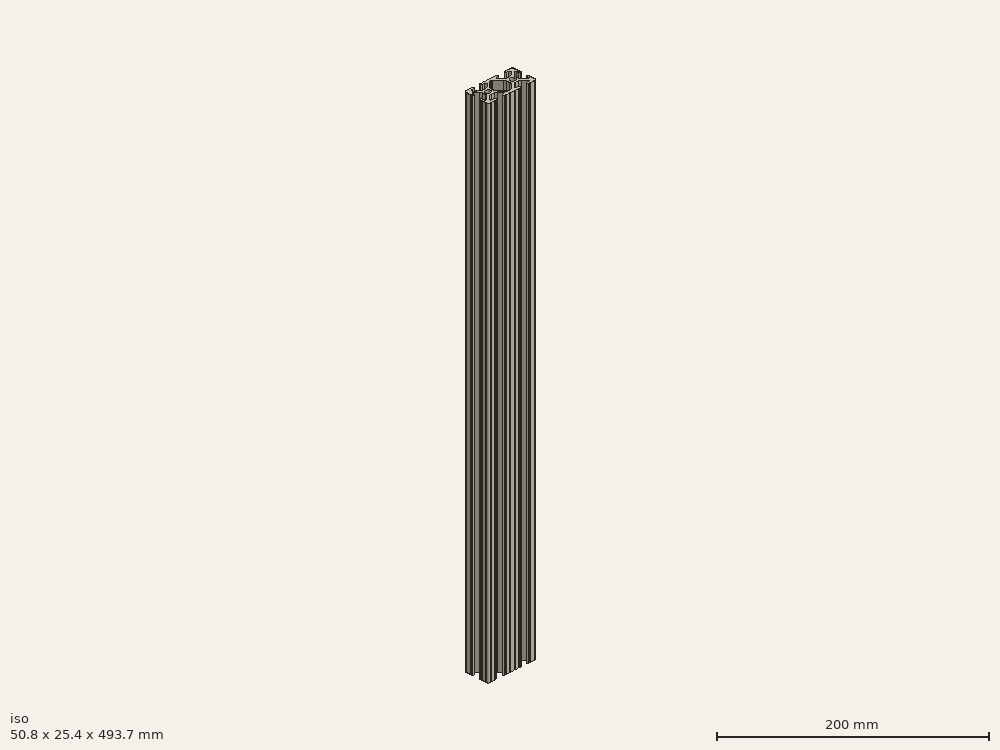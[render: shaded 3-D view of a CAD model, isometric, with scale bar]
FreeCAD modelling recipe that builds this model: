
FCSTD DOCUMENT  (FreeCAD 0.18R4 (GitTag))
Label: 1020-19p438
License: All rights reserved
LicenseURL: http://en.wikipedia.org/wiki/All_rights_reserved
objects: Sketcher::SketchObject×1, Part::Extrusion×1
note: 2 computed .brp shape members not serialized (recipe doc carries the construction recipe); baked Part::Feature solids carry a one-line shape summary decoded from their .brp

FEATURE [Sketcher::SketchObject] Sketch162
  sketch-geometry (162):
    g0: LineSegment StartX=7.25951 StartY=3.86941 StartZ=0 EndX=1.54575 EndY=9.57277 EndZ=0
    g1: LineSegment StartX=8.41248 StartY=-10.4902 StartZ=0 EndX=6.28364 EndY=-10.4902 EndZ=0
    g2: ArcOfCircle CenterX=8.41255 CenterY=-11.651 CenterZ=0 NormalX=0 NormalY=0 NormalZ=1 AngleXU=0 Radius=1.04895 StartAngle=4.71239 EndAngle=6.28319
    g3: LineSegment StartX=5.53258 StartY=-8.66607 StartZ=0 EndX=8.80999 EndY=-5.41626 EndZ=0
    g4: LineSegment StartX=9.4615 StartY=-11.651 StartZ=0 EndX=9.4615 EndY=-11.5392 EndZ=0
    g5: ArcOfCircle CenterX=8.41248 CenterY=-11.5392 CenterZ=0 NormalX=0 NormalY=0 NormalZ=1 AngleXU=0 Radius=1.04902 StartAngle=1.15714e-07 EndAngle=1.5708
    g6: ArcOfCircle CenterX=6.28364 CenterY=-9.42351 CenterZ=0 NormalX=0 NormalY=0 NormalZ=1 AngleXU=0 Radius=1.06669 StartAngle=2.35197 EndAngle=4.71239
    g7: LineSegment StartX=-7.28286 StartY=-3.84586 StartZ=0 EndX=-1.67557 EndY=-9.56109 EndZ=0
    g8: LineSegment StartX=1.50403 StartY=-9.57645 StartZ=0 EndX=7.25205 EndY=-3.87684 EndZ=0
    g9: LineSegment StartX=-0.551457 StartY=-10.033 StartZ=0 EndX=0.3952 EndY=-10.033 EndZ=0
    g10: LineSegment StartX=-1.54575 StartY=9.57277 StartZ=0 EndX=-7.25951 EndY=3.86941 EndZ=0
    g11: ArcOfCircle CenterX=0.3952 CenterY=-8.4582 CenterZ=0 NormalX=0 NormalY=0 NormalZ=1 AngleXU=0 Radius=1.5748 StartAngle=4.71239 EndAngle=5.49356
    g12: ArcOfCircle CenterX=5.0165 CenterY=-1.6223 CenterZ=0 NormalX=0 NormalY=0 NormalZ=1 AngleXU=0 Radius=3.175 StartAngle=5.49356 EndAngle=6.28319
    g13: LineSegment StartX=8.1915 StartY=-1.6223 StartZ=0 EndX=8.1915 EndY=1.6223 EndZ=0
    g14: LineSegment StartX=0.433213 StartY=10.033 StartZ=0 EndX=-0.433213 EndY=10.033 EndZ=0
    g15: ArcOfCircle CenterX=-0.551456 CenterY=-8.4582 CenterZ=0 NormalX=0 NormalY=0 NormalZ=1 AngleXU=0 Radius=1.5748 StartAngle=3.91746 EndAngle=4.71239
    g16: ArcOfCircle CenterX=-5.0165 CenterY=1.6223 CenterZ=0 NormalX=0 NormalY=0 NormalZ=1 AngleXU=0 Radius=3.175 StartAngle=2.35528 EndAngle=3.14159
    g17: ArcOfCircle CenterX=-0.433213 CenterY=8.4582 CenterZ=0 NormalX=0 NormalY=0 NormalZ=1 AngleXU=0 Radius=1.5748 StartAngle=1.5708 EndAngle=2.35528
    g18: ArcOfCircle CenterX=5.0165 CenterY=1.6223 CenterZ=0 NormalX=0 NormalY=0 NormalZ=1 AngleXU=0 Radius=3.175 StartAngle=2.15656e-07 EndAngle=0.78631
    g19: Circle CenterX=12.7 CenterY=-2.5e-15 CenterZ=0 NormalX=0 NormalY=0 NormalZ=-1 AngleXU=0 Radius=2.6035
    g20: Circle CenterX=-12.7 CenterY=2.5e-15 CenterZ=0 NormalX=0 NormalY=0 NormalZ=-1 AngleXU=0 Radius=2.6035
    g21: LineSegment StartX=-8.1915 StartY=1.6223 StartZ=0 EndX=-8.1915 EndY=-1.6223 EndZ=0
    g22: LineSegment StartX=-2.13358 StartY=-12.7 StartZ=0 EndX=2.13358 EndY=-12.7 EndZ=0
    g23: ArcOfCircle CenterX=-5.0165 CenterY=-1.6223 CenterZ=0 NormalX=0 NormalY=0 NormalZ=1 AngleXU=0 Radius=3.175 StartAngle=3.14159 EndAngle=3.91746
    g24: LineSegment StartX=3.14958 StartY=-12.7 StartZ=0 EndX=6.3669 EndY=-12.7 EndZ=0
    g25: ArcOfCircle CenterX=6.8749 CenterY=-12.7 CenterZ=0 NormalX=0 NormalY=0 NormalZ=1 AngleXU=0 Radius=0.508 StartAngle=0 EndAngle=3.14159
    g26: LineSegment StartX=-6.28939 StartY=-10.4902 StartZ=0 EndX=-8.41248 EndY=-10.4902 EndZ=0
    g27: LineSegment StartX=-8.41255 StartY=-12.7 StartZ=0 EndX=-7.38288 EndY=-12.7 EndZ=0
    g28: ArcOfCircle CenterX=0.433213 CenterY=8.4582 CenterZ=0 NormalX=0 NormalY=0 NormalZ=1 AngleXU=0 Radius=1.5748 StartAngle=0.78631 EndAngle=1.5708
    g29: ArcOfCircle CenterX=2.64158 CenterY=-12.7 CenterZ=0 NormalX=0 NormalY=0 NormalZ=1 AngleXU=0 Radius=0.508 StartAngle=0 EndAngle=3.14159
    g30: ArcOfCircle CenterX=-16.9875 CenterY=-11.5392 CenterZ=0 NormalX=0 NormalY=0 NormalZ=1 AngleXU=0 Radius=1.04902 StartAngle=1.16223e-07 EndAngle=1.5708
    g31: LineSegment StartX=-8.81696 StartY=-5.44724 StartZ=0 EndX=-5.56415 EndY=-8.76265 EndZ=0
    g32: LineSegment StartX=-16.9875 StartY=-10.4902 StartZ=0 EndX=-19.1164 EndY=-10.4902 EndZ=0
    g33: ArcOfCircle CenterX=-11.0833 CenterY=-7.6708 CenterZ=0 NormalX=0 NormalY=0 NormalZ=1 AngleXU=0 Radius=3.175 StartAngle=0.775866 EndAngle=1.5708
    g34: ArcOfCircle CenterX=-14.3449 CenterY=-7.6708 CenterZ=0 NormalX=0 NormalY=0 NormalZ=1 AngleXU=0 Radius=3.175 StartAngle=1.5708 EndAngle=2.3692
    g35: ArcOfCircle CenterX=-19.1164 CenterY=-9.4742 CenterZ=0 NormalX=0 NormalY=0 NormalZ=1 AngleXU=0 Radius=1.016 StartAngle=2.3692 EndAngle=4.71239
    g36: ArcOfCircle CenterX=-8.41248 CenterY=-11.5392 CenterZ=0 NormalX=0 NormalY=0 NormalZ=1 AngleXU=0 Radius=1.04902 StartAngle=1.5708 EndAngle=3.14159
    g37: LineSegment StartX=7.3829 StartY=-12.7 StartZ=0 EndX=8.41255 EndY=-12.7 EndZ=0
    g38: ArcOfCircle CenterX=-8.41255 CenterY=-11.651 CenterZ=0 NormalX=0 NormalY=0 NormalZ=1 AngleXU=0 Radius=1.04895 StartAngle=3.14159 EndAngle=4.71239
    g39: ArcOfCircle CenterX=14.3545 CenterY=-7.6708 CenterZ=0 NormalX=0 NormalY=0 NormalZ=1 AngleXU=0 Radius=3.175 StartAngle=0.789627 EndAngle=1.5708
    g40: ArcOfCircle CenterX=20.3835 CenterY=-1.55362 CenterZ=0 NormalX=0 NormalY=0 NormalZ=1 AngleXU=0 Radius=3.175 StartAngle=3.14159 EndAngle=3.93122
    g41: LineSegment StartX=23.1902 StartY=6.498 StartZ=0 EndX=23.1902 EndY=4.28752 EndZ=0
    g42: LineSegment StartX=-14.3449 StartY=-4.4958 StartZ=0 EndX=-11.0833 EndY=-4.4958 EndZ=0
    g43: LineSegment StartX=-19.8441 StartY=-8.76517 StartZ=0 EndX=-16.619 EndY=-5.45511 EndZ=0
    g44: LineSegment StartX=-6.36688 StartY=-12.7 StartZ=0 EndX=-3.14958 EndY=-12.7 EndZ=0
    g45: ArcOfCircle CenterX=-6.28939 CenterY=-9.4742 CenterZ=0 NormalX=0 NormalY=0 NormalZ=1 AngleXU=0 Radius=1.016 StartAngle=4.71239 EndAngle=7.05905
    g46: LineSegment StartX=-9.4615 StartY=-11.5392 StartZ=0 EndX=-9.4615 EndY=-11.6511 EndZ=0
    g47: ArcOfCircle CenterX=-6.87488 CenterY=-12.7 CenterZ=0 NormalX=0 NormalY=0 NormalZ=1 AngleXU=0 Radius=0.508 StartAngle=0 EndAngle=3.14159
    g48: LineSegment StartX=-15.9385 StartY=-11.651 StartZ=0 EndX=-15.9385 EndY=-11.5392 EndZ=0
    g49: ArcOfCircle CenterX=-2.64158 CenterY=-12.7 CenterZ=0 NormalX=0 NormalY=0 NormalZ=1 AngleXU=0 Radius=0.508 StartAngle=0 EndAngle=3.14159
    g50: ArcOfCircle CenterX=22.1596 CenterY=-6.33474 CenterZ=0 NormalX=0 NormalY=0 NormalZ=1 AngleXU=0 Radius=1.03057 StartAngle=3.93122 EndAngle=6.28319
    g51: ArcOfCircle CenterX=25.4 CenterY=5.82513 CenterZ=0 NormalX=0 NormalY=0 NormalZ=1 AngleXU=0 Radius=0.508 StartAngle=1.5708 EndAngle=4.71239
    g52: LineSegment StartX=25.4 StartY=6.33313 StartZ=0 EndX=25.4 EndY=9.5504 EndZ=0
    g53: LineSegment StartX=19.0331 StartY=-12.7 StartZ=0 EndX=22.2504 EndY=-12.7 EndZ=0
    g54: ArcOfCircle CenterX=20.3835 CenterY=1.69518 CenterZ=0 NormalX=0 NormalY=0 NormalZ=1 AngleXU=0 Radius=3.175 StartAngle=2.35528 EndAngle=3.14159
    g55: LineSegment StartX=16.9875 StartY=-12.7 StartZ=0 EndX=18.0171 EndY=-12.7 EndZ=0
    g56: ArcOfCircle CenterX=23.2918 CenterY=10.5918 CenterZ=0 NormalX=0 NormalY=0 NormalZ=1 AngleXU=0 Radius=2.1082 StartAngle=6.27114 EndAngle=7.86603
    g57: ArcOfCircle CenterX=24.2392 CenterY=-4.28752 CenterZ=0 NormalX=0 NormalY=0 NormalZ=1 AngleXU=0 Radius=1.04902 StartAngle=1.5708 EndAngle=3.14159
    g58: ArcOfCircle CenterX=24.401 CenterY=-4.23752 CenterZ=0 NormalX=0 NormalY=0 NormalZ=1 AngleXU=0 Radius=0.99902 StartAngle=1.41033e-07 EndAngle=1.5708
    g59: LineSegment StartX=16.59 StartY=-5.41626 StartZ=0 EndX=19.8674 EndY=-8.66607 EndZ=0
    g60: ArcOfCircle CenterX=16.9875 CenterY=-11.5392 CenterZ=0 NormalX=0 NormalY=0 NormalZ=1 AngleXU=0 Radius=1.04902 StartAngle=1.5708 EndAngle=3.14159
    g61: LineSegment StartX=22.2504 StartY=12.7 StartZ=0 EndX=19.0331 EndY=12.7 EndZ=0
    g62: ArcOfCircle CenterX=23.2918 CenterY=-10.5918 CenterZ=0 NormalX=0 NormalY=0 NormalZ=1 AngleXU=0 Radius=2.1082 StartAngle=4.70034 EndAngle=6.29523
    g63: ArcOfCircle CenterX=11.0455 CenterY=-7.6708 CenterZ=0 NormalX=0 NormalY=0 NormalZ=1 AngleXU=0 Radius=3.175 StartAngle=1.5708 EndAngle=2.35197
    g64: ArcOfCircle CenterX=22.7584 CenterY=12.7 CenterZ=0 NormalX=0 NormalY=0 NormalZ=1 AngleXU=0 Radius=0.508 StartAngle=3.14159 EndAngle=6.28288
    g65: LineSegment StartX=19.1164 StartY=-10.4902 StartZ=0 EndX=16.9875 EndY=-10.4902 EndZ=0
    g66: ArcOfCircle CenterX=22.7584 CenterY=-12.7 CenterZ=0 NormalX=0 NormalY=0 NormalZ=1 AngleXU=0 Radius=0.508 StartAngle=0.000301216 EndAngle=3.14159
    g67: ArcOfCircle CenterX=16.9875 CenterY=11.651 CenterZ=0 NormalX=0 NormalY=0 NormalZ=1 AngleXU=0 Radius=1.04902 StartAngle=1.5708 EndAngle=3.14159
    g68: ArcOfCircle CenterX=24.351 CenterY=4.28752 CenterZ=0 NormalX=0 NormalY=0 NormalZ=1 AngleXU=0 Radius=1.04902 StartAngle=4.71239 EndAngle=6.28319
    g69: ArcOfCircle CenterX=19.1164 CenterY=9.4742 CenterZ=0 NormalX=0 NormalY=0 NormalZ=1 AngleXU=0 Radius=1.016 StartAngle=5.49688 EndAngle=7.85398
    g70: LineSegment StartX=19.8341 StartY=8.75512 StartZ=0 EndX=16.4966 EndY=5.42369 EndZ=0
    g71: LineSegment StartX=18.0171 StartY=12.7 StartZ=0 EndX=16.9875 EndY=12.7 EndZ=0
    g72: ArcOfCircle CenterX=18.5251 CenterY=-12.7 CenterZ=0 NormalX=0 NormalY=0 NormalZ=1 AngleXU=0 Radius=0.508 StartAngle=0 EndAngle=3.14159
    g73: LineSegment StartX=15.9384 StartY=11.651 StartZ=0 EndX=15.9384 EndY=11.5392 EndZ=0
    g74: LineSegment StartX=16.9875 StartY=10.4902 StartZ=0 EndX=19.1164 EndY=10.4902 EndZ=0
    g75: LineSegment StartX=11.0455 StartY=-4.4958 StartZ=0 EndX=14.3545 EndY=-4.4958 EndZ=0
    g76: ArcOfCircle CenterX=14.2536 CenterY=7.6708 CenterZ=0 NormalX=0 NormalY=0 NormalZ=1 AngleXU=0 Radius=3.175 StartAngle=4.71239 EndAngle=5.49688
    g77: ArcOfCircle CenterX=25.4 CenterY=-5.82508 CenterZ=0 NormalX=0 NormalY=0 NormalZ=1 AngleXU=0 Radius=0.508 StartAngle=1.5708 EndAngle=4.71239
    g78: LineSegment StartX=18.1405 StartY=3.94229 StartZ=0 EndX=21.4316 EndY=7.22739 EndZ=0
    g79: LineSegment StartX=25.4 StartY=-5.31708 StartZ=0 EndX=25.4 EndY=-4.23752 EndZ=0
    g80: LineSegment StartX=14.2536 StartY=4.4958 StartZ=0 EndX=11.1464 EndY=4.4958 EndZ=0
    g81: ArcOfCircle CenterX=18.5251 CenterY=12.7 CenterZ=0 NormalX=0 NormalY=0 NormalZ=1 AngleXU=0 Radius=0.508 StartAngle=3.14159 EndAngle=6.28319
    g82: LineSegment StartX=23.1902 StartY=-4.28752 StartZ=0 EndX=23.1902 EndY=-6.33474 EndZ=0
    g83: LineSegment StartX=24.401 StartY=-3.2385 StartZ=0 EndX=24.2392 EndY=-3.2385 EndZ=0
    g84: ArcOfCircle CenterX=22.1596 CenterY=6.498 CenterZ=0 NormalX=0 NormalY=0 NormalZ=1 AngleXU=0 Radius=1.03057 StartAngle=0 EndAngle=2.35528
    g85: LineSegment StartX=15.9385 StartY=-11.5392 StartZ=0 EndX=15.9385 EndY=-11.6511 EndZ=0
    g86: LineSegment StartX=25.4 StartY=4.28752 StartZ=0 EndX=25.4 EndY=5.31713 EndZ=0
    g87: ArcOfCircle CenterX=11.1464 CenterY=7.6708 CenterZ=0 NormalX=0 NormalY=0 NormalZ=1 AngleXU=0 Radius=3.175 StartAngle=3.9279 EndAngle=4.71239
    g88: LineSegment StartX=8.90339 StartY=5.42369 StartZ=0 EndX=5.56588 EndY=8.75512 EndZ=0
    g89: LineSegment StartX=21.434 StartY=-7.06654 StartZ=0 EndX=18.148 EndY=-3.80816 EndZ=0
    g90: ArcOfCircle CenterX=25.4 CenterY=10.0584 CenterZ=0 NormalX=0 NormalY=0 NormalZ=1 AngleXU=0 Radius=0.508 StartAngle=1.5711 EndAngle=4.71239
    g91: ArcOfCircle CenterX=16.9875 CenterY=-11.651 CenterZ=0 NormalX=0 NormalY=0 NormalZ=1 AngleXU=0 Radius=1.04895 StartAngle=3.14159 EndAngle=4.71239
    g92: ArcOfCircle CenterX=19.1164 CenterY=-9.42352 CenterZ=0 NormalX=0 NormalY=0 NormalZ=1 AngleXU=0 Radius=1.06668 StartAngle=4.71239 EndAngle=7.07281
    g93: ArcOfCircle CenterX=24.2392 CenterY=4.28752 CenterZ=0 NormalX=0 NormalY=0 NormalZ=1 AngleXU=0 Radius=1.04902 StartAngle=3.14159 EndAngle=4.71239
    g94: ArcOfCircle CenterX=16.9875 CenterY=11.5392 CenterZ=0 NormalX=0 NormalY=0 NormalZ=1 AngleXU=0 Radius=1.04902 StartAngle=3.14159 EndAngle=4.71239
    g95: ArcOfCircle CenterX=25.4 CenterY=-10.0584 CenterZ=0 NormalX=0 NormalY=0 NormalZ=1 AngleXU=0 Radius=0.508 StartAngle=1.5708 EndAngle=4.71209
    g96: ArcOfCircle CenterX=6.87487 CenterY=12.7 CenterZ=0 NormalX=0 NormalY=0 NormalZ=1 AngleXU=0 Radius=0.508 StartAngle=3.14159 EndAngle=6.28319
    g97: LineSegment StartX=25.4 StartY=-9.5504 StartZ=0 EndX=25.4 EndY=-6.33308 EndZ=0
    g98: LineSegment StartX=17.2085 StartY=-1.55362 StartZ=0 EndX=17.2085 EndY=1.69518 EndZ=0
    g99: LineSegment StartX=-9.46155 StartY=11.651 StartZ=0 EndX=-9.46155 EndY=11.5392 EndZ=0
    g100: LineSegment StartX=24.2392 StartY=3.2385 StartZ=0 EndX=24.351 EndY=3.2385 EndZ=0
    g101: LineSegment StartX=-8.41253 StartY=10.4902 StartZ=0 EndX=-6.28939 EndY=10.4902 EndZ=0
    g102: ArcOfCircle CenterX=-10.8409 CenterY=7.6708 CenterZ=0 NormalX=0 NormalY=0 NormalZ=1 AngleXU=0 Radius=3.175 StartAngle=4.71239 EndAngle=5.49688
    g103: LineSegment StartX=-19.1164 StartY=10.4902 StartZ=0 EndX=-16.9875 EndY=10.4902 EndZ=0
    g104: LineSegment StartX=-10.8409 StartY=4.4958 StartZ=0 EndX=-14.1026 EndY=4.4958 EndZ=0
    g105: LineSegment StartX=-16.1879 StartY=5.27664 StartZ=0 EndX=-19.8682 EndY=8.48225 EndZ=0
    g106: LineSegment StartX=-7.38291 StartY=12.7 StartZ=0 EndX=-8.41253 EndY=12.7 EndZ=0
    g107: ArcOfCircle CenterX=-6.28939 CenterY=9.34546 CenterZ=0 NormalX=0 NormalY=0 NormalZ=1 AngleXU=0 Radius=1.14474 StartAngle=5.49688 EndAngle=7.85398
    g108: LineSegment StartX=6.28364 StartY=10.4902 StartZ=0 EndX=8.41253 EndY=10.4902 EndZ=0
    g109: ArcOfCircle CenterX=8.41253 CenterY=11.651 CenterZ=0 NormalX=0 NormalY=0 NormalZ=1 AngleXU=0 Radius=1.04902 StartAngle=4.29175e-07 EndAngle=1.5708
    g110: LineSegment StartX=9.46155 StartY=11.5392 StartZ=0 EndX=9.46155 EndY=11.651 EndZ=0
    g111: ArcOfCircle CenterX=-14.1026 CenterY=7.6708 CenterZ=0 NormalX=0 NormalY=0 NormalZ=1 AngleXU=0 Radius=3.175 StartAngle=3.99583 EndAngle=4.71239
    g112: LineSegment StartX=-5.48068 StartY=8.53527 StartZ=0 EndX=-8.59793 EndY=5.42369 EndZ=0
    g113: ArcOfCircle CenterX=-19.1164 CenterY=9.34546 CenterZ=0 NormalX=0 NormalY=0 NormalZ=1 AngleXU=0 Radius=1.14474 StartAngle=1.5708 EndAngle=3.99583
    g114: LineSegment StartX=8.41253 StartY=12.7 StartZ=0 EndX=7.38287 EndY=12.7 EndZ=0
    g115: LineSegment StartX=-3.14958 StartY=12.7 StartZ=0 EndX=-6.36691 EndY=12.7 EndZ=0
    g116: ArcOfCircle CenterX=-8.41253 CenterY=11.5392 CenterZ=0 NormalX=0 NormalY=0 NormalZ=1 AngleXU=0 Radius=1.04902 StartAngle=3.14159 EndAngle=4.71239
    g117: ArcOfCircle CenterX=8.41253 CenterY=11.5392 CenterZ=0 NormalX=0 NormalY=0 NormalZ=1 AngleXU=0 Radius=1.04902 StartAngle=4.71239 EndAngle=6.28319
    g118: ArcOfCircle CenterX=-6.87491 CenterY=12.7 CenterZ=0 NormalX=0 NormalY=0 NormalZ=1 AngleXU=0 Radius=0.508 StartAngle=3.14159 EndAngle=6.28319
    g119: ArcOfCircle CenterX=-8.41253 CenterY=11.651 CenterZ=0 NormalX=0 NormalY=0 NormalZ=1 AngleXU=0 Radius=1.04902 StartAngle=1.5708 EndAngle=3.14159
    g120: ArcOfCircle CenterX=-2.64159 CenterY=12.7 CenterZ=0 NormalX=0 NormalY=0 NormalZ=1 AngleXU=0 Radius=0.507987 StartAngle=3.14159 EndAngle=6.28319
    g121: ArcOfCircle CenterX=6.28364 CenterY=9.4742 CenterZ=0 NormalX=0 NormalY=0 NormalZ=1 AngleXU=0 Radius=1.016 StartAngle=1.5708 EndAngle=3.9279
    g122: LineSegment StartX=2.13361 StartY=12.7 StartZ=0 EndX=-2.13361 EndY=12.7 EndZ=0
    g123: LineSegment StartX=6.36687 StartY=12.7 StartZ=0 EndX=3.14961 EndY=12.7 EndZ=0
    g124: ArcOfCircle CenterX=-24.401 CenterY=4.23752 CenterZ=0 NormalX=0 NormalY=0 NormalZ=1 AngleXU=0 Radius=0.99902 StartAngle=3.14159 EndAngle=4.71239
    g125: LineSegment StartX=-16.9875 StartY=12.7 StartZ=0 EndX=-18.0171 EndY=12.7 EndZ=0
    g126: LineSegment StartX=-24.401 StartY=3.2385 StartZ=0 EndX=-24.1892 EndY=3.2385 EndZ=0
    g127: ArcOfCircle CenterX=2.64161 CenterY=12.7 CenterZ=0 NormalX=0 NormalY=0 NormalZ=1 AngleXU=0 Radius=0.508 StartAngle=3.14159 EndAngle=6.28319
    g128: ArcOfCircle CenterX=-22.2207 CenterY=-6.67687 CenterZ=0 NormalX=0 NormalY=0 NormalZ=1 AngleXU=0 Radius=0.969476 StartAngle=3.14159 EndAngle=5.51079
    g129: LineSegment StartX=-18.1094 StartY=-3.8465 StartZ=0 EndX=-21.5263 EndY=-7.35342 EndZ=0
    g130: LineSegment StartX=-17.2085 StartY=1.63081 StartZ=0 EndX=-17.2085 EndY=-1.63081 EndZ=0
    g131: ArcOfCircle CenterX=-22.2207 CenterY=6.15588 CenterZ=0 NormalX=0 NormalY=0 NormalZ=1 AngleXU=0 Radius=0.969476 StartAngle=0.854233 EndAngle=3.14159
    g132: LineSegment StartX=-24.1892 StartY=-3.2385 StartZ=0 EndX=-24.401 EndY=-3.2385 EndZ=0
    g133: ArcOfCircle CenterX=-25.4 CenterY=10.0584 CenterZ=0 NormalX=0 NormalY=0 NormalZ=1 AngleXU=0 Radius=0.508 StartAngle=4.71239 EndAngle=7.85368
    g134: LineSegment StartX=-23.1902 StartY=-6.67687 StartZ=0 EndX=-23.1902 EndY=-4.23752 EndZ=0
    g135: ArcOfCircle CenterX=-20.3835 CenterY=-1.63081 CenterZ=0 NormalX=0 NormalY=0 NormalZ=1 AngleXU=0 Radius=3.175 StartAngle=5.51079 EndAngle=6.28319
    g136: ArcOfCircle CenterX=-24.1892 CenterY=-4.23752 CenterZ=0 NormalX=0 NormalY=0 NormalZ=1 AngleXU=0 Radius=0.99902 StartAngle=1.41033e-07 EndAngle=1.5708
    g137: ArcOfCircle CenterX=-25.4 CenterY=5.82508 CenterZ=0 NormalX=0 NormalY=0 NormalZ=1 AngleXU=0 Radius=0.508 StartAngle=4.71239 EndAngle=7.85398
    g138: LineSegment StartX=-23.1902 StartY=4.23752 StartZ=0 EndX=-23.1902 EndY=6.15588 EndZ=0
    g139: LineSegment StartX=-15.9384 StartY=11.5392 StartZ=0 EndX=-15.9384 EndY=11.651 EndZ=0
    g140: ArcOfCircle CenterX=-22.7584 CenterY=12.7 CenterZ=0 NormalX=0 NormalY=0 NormalZ=1 AngleXU=0 Radius=0.508 StartAngle=3.14189 EndAngle=6.28319
    g141: LineSegment StartX=-19.0331 StartY=12.7 StartZ=0 EndX=-22.2504 EndY=12.7 EndZ=0
    g142: ArcOfCircle CenterX=-16.9875 CenterY=11.651 CenterZ=0 NormalX=0 NormalY=0 NormalZ=1 AngleXU=0 Radius=1.04902 StartAngle=4.28571e-07 EndAngle=1.5708
    g143: ArcOfCircle CenterX=-18.5251 CenterY=12.7 CenterZ=0 NormalX=0 NormalY=0 NormalZ=1 AngleXU=0 Radius=0.508 StartAngle=3.14159 EndAngle=6.28319
    g144: ArcOfCircle CenterX=-24.1892 CenterY=4.23752 CenterZ=0 NormalX=0 NormalY=0 NormalZ=1 AngleXU=0 Radius=0.99902 StartAngle=4.71239 EndAngle=6.28319
    g145: LineSegment StartX=-25.4 StartY=5.31708 StartZ=0 EndX=-25.4 EndY=4.23752 EndZ=0
    g146: ArcOfCircle CenterX=-16.9875 CenterY=11.5392 CenterZ=0 NormalX=0 NormalY=0 NormalZ=1 AngleXU=0 Radius=1.04902 StartAngle=4.71239 EndAngle=6.28319
    g147: LineSegment StartX=-21.584 StartY=6.88693 StartZ=0 EndX=-18.2982 EndY=4.02497 EndZ=0
    g148: ArcOfCircle CenterX=-20.3835 CenterY=1.63081 CenterZ=0 NormalX=0 NormalY=0 NormalZ=1 AngleXU=0 Radius=3.175 StartAngle=0 EndAngle=0.854233
    g149: ArcOfCircle CenterX=-23.2918 CenterY=10.5918 CenterZ=0 NormalX=0 NormalY=0 NormalZ=1 AngleXU=0 Radius=2.1082 StartAngle=1.55875 EndAngle=3.15364
    g150: LineSegment StartX=-25.4 StartY=9.5504 StartZ=0 EndX=-25.4 EndY=6.33308 EndZ=0
    g151: LineSegment StartX=-25.4 StartY=-4.23752 StartZ=0 EndX=-25.4 EndY=-5.31708 EndZ=0
    g152: ArcOfCircle CenterX=-23.2918 CenterY=-10.5918 CenterZ=0 NormalX=0 NormalY=0 NormalZ=1 AngleXU=0 Radius=2.1082 StartAngle=3.12954 EndAngle=4.72444
    g153: ArcOfCircle CenterX=-22.7584 CenterY=-12.7 CenterZ=0 NormalX=0 NormalY=0 NormalZ=1 AngleXU=0 Radius=0.508 StartAngle=0 EndAngle=3.14129
    g154: LineSegment StartX=-18.0171 StartY=-12.7 StartZ=0 EndX=-16.9875 EndY=-12.7 EndZ=0
    g155: ArcOfCircle CenterX=-25.4 CenterY=-10.0584 CenterZ=0 NormalX=0 NormalY=0 NormalZ=1 AngleXU=0 Radius=0.508 StartAngle=4.71269 EndAngle=7.85398
    g156: LineSegment StartX=-22.2504 StartY=-12.7 StartZ=0 EndX=-19.0331 EndY=-12.7 EndZ=0
    g157: ArcOfCircle CenterX=-16.9875 CenterY=-11.651 CenterZ=0 NormalX=0 NormalY=0 NormalZ=1 AngleXU=0 Radius=1.04895 StartAngle=4.71239 EndAngle=6.28319
    g158: ArcOfCircle CenterX=-24.401 CenterY=-4.23752 CenterZ=0 NormalX=0 NormalY=0 NormalZ=1 AngleXU=0 Radius=0.99902 StartAngle=1.5708 EndAngle=3.14159
    g159: ArcOfCircle CenterX=-25.4 CenterY=-5.82513 CenterZ=0 NormalX=0 NormalY=0 NormalZ=1 AngleXU=0 Radius=0.508051 StartAngle=4.71239 EndAngle=7.85398
    g160: ArcOfCircle CenterX=-18.5251 CenterY=-12.7 CenterZ=0 NormalX=0 NormalY=0 NormalZ=1 AngleXU=0 Radius=0.508 StartAngle=0 EndAngle=3.14159
    g161: LineSegment StartX=-25.4 StartY=-6.33319 StartZ=0 EndX=-25.4 EndY=-9.5504 EndZ=0
  constraints (160):
    c: Coincident(g161,g155)
    c: Coincident(g159,g161)
    c: Coincident(g151,g159)
    c: Coincident(g158,g151)
    c: Coincident(g124,g145)
    c: Coincident(g137,g145)
    c: Coincident(g137,g150)
    c: Coincident(g133,g150)
    c: Coincident(g152,g155)
    c: Coincident(g149,g133)
    c: Coincident(g158,g132)
    c: Coincident(g124,g126)
    c: Coincident(g136,g132)
    c: Coincident(g144,g126)
    c: Coincident(g153,g152)
    c: Coincident(g140,g149)
    c: Coincident(g134,g128)
    c: Coincident(g134,g136)
    c: Coincident(g138,g144)
    c: Coincident(g131,g138)
    c: Coincident(g153,g156)
    c: Coincident(g141,g140)
    c: Coincident(g131,g147)
    c: Coincident(g129,g128)
    c: Coincident(g105,g113)
    c: Coincident(g35,g43)
    c: Coincident(g35,g32)
    c: Coincident(g113,g103)
    c: Coincident(g156,g160)
    c: Coincident(g143,g141)
    c: Coincident(g147,g148)
    c: Coincident(g135,g129)
    c: Coincident(g154,g160)
    c: Coincident(g143,g125)
    c: Coincident(g130,g135)
    c: Coincident(g130,g148)
    c: Coincident(g154,g157)
    c: Coincident(g32,g30)
    c: Coincident(g103,g146)
    c: Coincident(g142,g125)
    c: Coincident(g43,g34)
    c: Coincident(g111,g105)
    c: Coincident(g157,g48)
    c: Coincident(g48,g30)
    c: Coincident(g139,g146)
    c: Coincident(g139,g142)
    c: Coincident(g42,g34)
    c: Coincident(g104,g111)
    c: Coincident(g33,g42)
    c: Coincident(g102,g104)
    c: Coincident(g38,g46)
    c: Coincident(g46,g36)
    c: Coincident(g99,g116)
    c: Coincident(g119,g99)
    c: Coincident(g33,g31)
    c: Coincident(g102,g112)
    c: Coincident(g27,g38)
    c: Coincident(g36,g26)
    c: Coincident(g116,g101)
    c: Coincident(g106,g119)
    c: Coincident(g21,g23)
    c: Coincident(g21,g16)
    c: Coincident(g27,g47)
    c: Coincident(g106,g118)
    c: Coincident(g23,g7)
    c: Coincident(g10,g16)
    c: Coincident(g44,g47)
    c: Coincident(g118,g115)
    c: Coincident(g45,g26)
    c: Coincident(g107,g101)
    c: Coincident(g45,g31)
    c: Coincident(g112,g107)
    c: Coincident(g44,g49)
    c: Coincident(g120,g115)
    c: Coincident(g22,g49)
    c: Coincident(g122,g120)
    c: Coincident(g15,g7)
    c: Coincident(g10,g17)
    c: Coincident(g9,g15)
    c: Coincident(g17,g14)
    c: Coincident(g9,g11)
    c: Coincident(g14,g28)
    c: Coincident(g8,g11)
    c: Coincident(g0,g28)
    c: Coincident(g29,g22)
    c: Coincident(g122,g127)
    c: Coincident(g24,g29)
    c: Coincident(g123,g127)
    c: Coincident(g3,g6)
    c: Coincident(g88,g121)
    c: Coincident(g1,g6)
    c: Coincident(g108,g121)
    c: Coincident(g25,g24)
    c: Coincident(g96,g123)
    c: Coincident(g8,g12)
    c: Coincident(g18,g0)
    c: Coincident(g25,g37)
    c: Coincident(g96,g114)
    c: Coincident(g12,g13)
    c: Coincident(g18,g13)
    c: Coincident(g2,g37)
    c: Coincident(g5,g1)
    c: Coincident(g117,g108)
    c: Coincident(g109,g114)
    c: Coincident(g3,g63)
    c: Coincident(g87,g88)
    c: Coincident(g2,g4)
    c: Coincident(g5,g4)
    c: Coincident(g117,g110)
    c: Coincident(g109,g110)
    c: Coincident(g75,g63)
    c: Coincident(g80,g87)
    c: Coincident(g80,g76)
    c: Coincident(g39,g75)
    c: Coincident(g85,g91)
    c: Coincident(g85,g60)
    c: Coincident(g73,g94)
    c: Coincident(g73,g67)
    c: Coincident(g70,g76)
    c: Coincident(g59,g39)
    c: Coincident(g55,g91)
    c: Coincident(g60,g65)
    c: Coincident(g94,g74)
    c: Coincident(g67,g71)
    c: Coincident(g40,g98)
    c: Coincident(g54,g98)
    c: Coincident(g55,g72)
    c: Coincident(g71,g81)
    c: Coincident(g78,g54)
    c: Coincident(g40,g89)
    c: Coincident(g53,g72)
    c: Coincident(g61,g81)
    c: Coincident(g65,g92)
    c: Coincident(g74,g69)
    c: Coincident(g70,g69)
    c: Coincident(g59,g92)
    c: Coincident(g84,g78)
    c: Coincident(g50,g89)
    c: Coincident(g53,g66)
    c: Coincident(g64,g61)
    c: Coincident(g82,g50)
    c: Coincident(g57,g82)
    c: Coincident(g41,g93)
    c: Coincident(g41,g84)
    c: Coincident(g62,g66)
    c: Coincident(g64,g56)
    c: Coincident(g57,g83)
    c: Coincident(g100,g93)
    c: Coincident(g100,g68)
    c: Coincident(g58,g83)
    c: Coincident(g62,g95)
    c: Coincident(g56,g90)
    c: Coincident(g97,g95)
    c: Coincident(g97,g77)
    c: Coincident(g77,g79)
    c: Coincident(g58,g79)
    c: Coincident(g68,g86)
    c: Coincident(g86,g51)
    c: Coincident(g51,g52)
    c: Coincident(g52,g90)
FEATURE [Part::Extrusion] Extrude
  Base = -> Sketch162
  Dir = (0,0,1)
  DirMode = 2
  FaceMakerClass = Part::FaceMakerBullseye
  LengthFwd = 493.725
  LengthRev = 0
  Solid = true
  Symmetric = false
